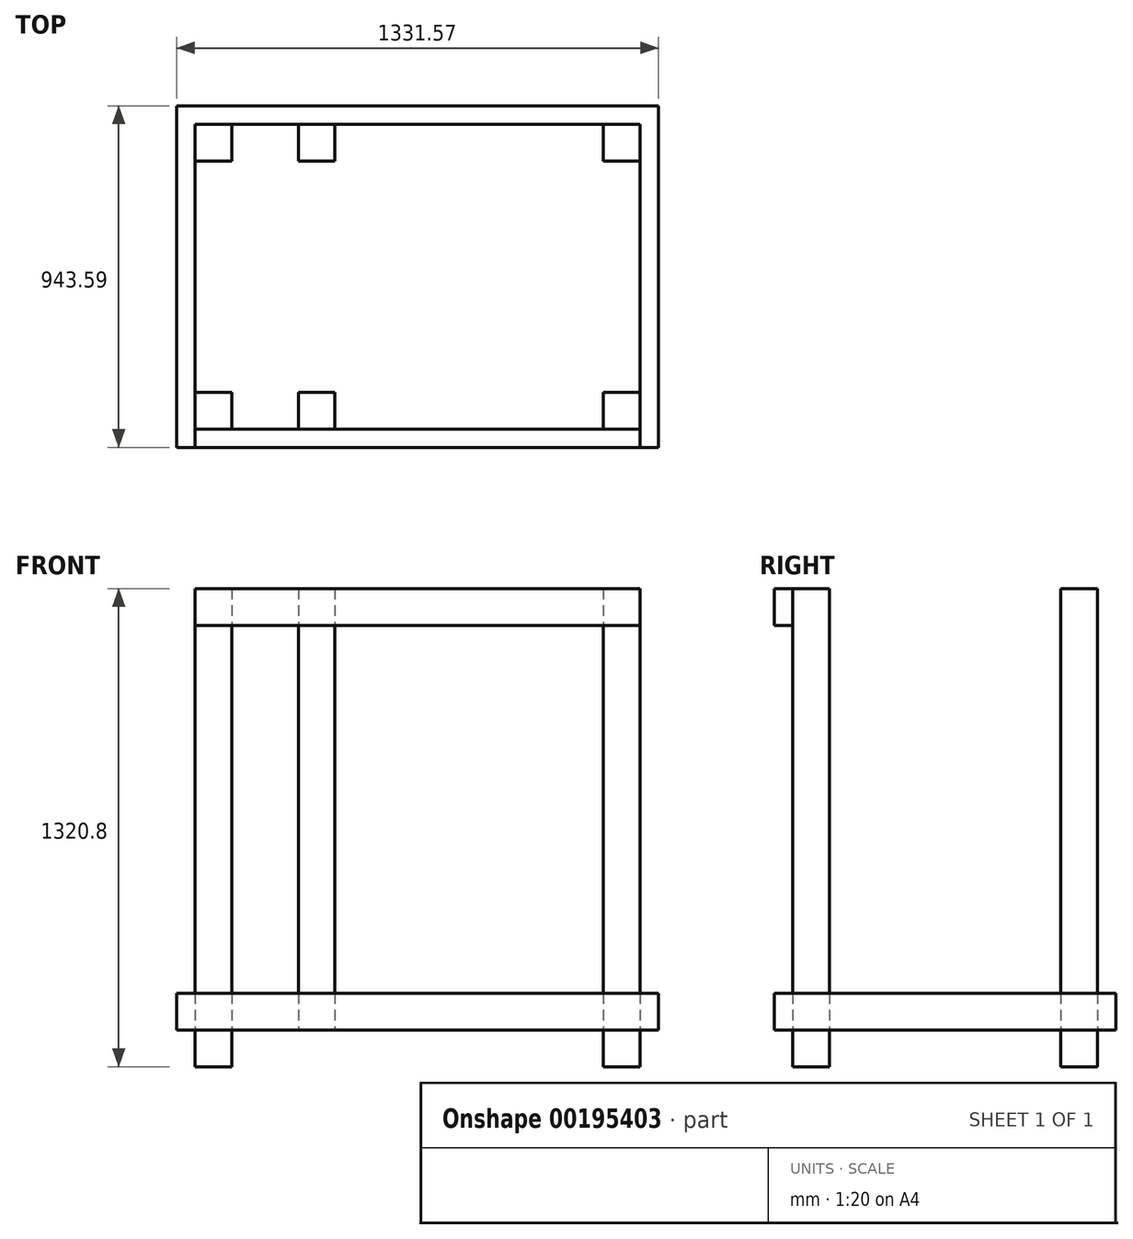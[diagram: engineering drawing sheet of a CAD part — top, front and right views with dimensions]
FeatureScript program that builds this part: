
annotation { "Feature Type Name" : "Feature", "Feature Type Description" : "" }
export const myFeature = defineFeature(function(context is Context, id is Id, definition is map)
    precondition{}
    {
        {
            var Q0;
            Q0=qCreatedBy(makeId("Top.planeOp"),FACE);
            var sketch = newSketch(context, id + "F0", { "sketchPlane" : qUnion([Q0])});
            skLineSegment(sketch, "E0.bottom", {"start": v(0, 0) * mm, "end": v(101.6, 0) * mm});
            skLineSegment(sketch, "E0.top", {"start": v(0, -101.6) * mm, "end": v(101.6, -101.6) * mm});
            skLineSegment(sketch, "E0.left", {"start": v(0, 0) * mm, "end": v(0, -101.6) * mm});
            skLineSegment(sketch, "E0.right", {"start": v(101.6, 0) * mm, "end": v(101.6, -101.6) * mm});
            skLineSegment(sketch, "E1.bottom", {"start": v(0, -740.39) * mm, "end": v(101.6, -740.39) * mm});
            skLineSegment(sketch, "E1.top", {"start": v(0, -841.99) * mm, "end": v(101.6, -841.99) * mm});
            skLineSegment(sketch, "E1.left", {"start": v(0, -740.39) * mm, "end": v(0, -841.99) * mm});
            skLineSegment(sketch, "E1.right", {"start": v(101.6, -740.39) * mm, "end": v(101.6, -841.99) * mm});
            skLineSegment(sketch, "E2.bottom", {"start": v(1128.37, -740.39) * mm, "end": v(1229.97, -740.39) * mm});
            skLineSegment(sketch, "E2.top", {"start": v(1128.37, -841.99) * mm, "end": v(1229.97, -841.99) * mm});
            skLineSegment(sketch, "E2.left", {"start": v(1128.37, -740.39) * mm, "end": v(1128.37, -841.99) * mm});
            skLineSegment(sketch, "E2.right", {"start": v(1229.97, -740.39) * mm, "end": v(1229.97, -841.99) * mm});
            skLineSegment(sketch, "E3.bottom", {"start": v(1128.37, -101.6) * mm, "end": v(1229.97, -101.6) * mm});
            skLineSegment(sketch, "E3.top", {"start": v(1128.37, 0) * mm, "end": v(1229.97, 0) * mm});
            skLineSegment(sketch, "E3.left", {"start": v(1128.37, -101.6) * mm, "end": v(1128.37, 0) * mm});
            skLineSegment(sketch, "E3.right", {"start": v(1229.97, -101.6) * mm, "end": v(1229.97, 0) * mm});
            skLineSegment(sketch, "E4.bottom", {"start": v(285.44, -740.39) * mm, "end": v(387.04, -740.39) * mm});
            skLineSegment(sketch, "E4.top", {"start": v(285.44, -841.99) * mm, "end": v(387.04, -841.99) * mm});
            skLineSegment(sketch, "E4.left", {"start": v(285.44, -740.39) * mm, "end": v(285.44, -841.99) * mm});
            skLineSegment(sketch, "E4.right", {"start": v(387.04, -740.39) * mm, "end": v(387.04, -841.99) * mm});
            skLineSegment(sketch, "E5.bottom", {"start": v(285.44, -101.6) * mm, "end": v(387.04, -101.6) * mm});
            skLineSegment(sketch, "E5.top", {"start": v(285.44, 0) * mm, "end": v(387.04, 0) * mm});
            skLineSegment(sketch, "E5.left", {"start": v(285.44, -101.6) * mm, "end": v(285.44, 0) * mm});
            skLineSegment(sketch, "E5.right", {"start": v(387.04, -101.6) * mm, "end": v(387.04, 0) * mm});
            skLineSegment(sketch, "E6.bottom", {"start": v(0, 0) * mm, "end": v(1229.97, 0) * mm});
            skLineSegment(sketch, "E6.top", {"start": v(0, 50.8) * mm, "end": v(1229.97, 50.8) * mm});
            skLineSegment(sketch, "E6.left", {"start": v(0, 0) * mm, "end": v(0, 50.8) * mm});
            skLineSegment(sketch, "E6.right", {"start": v(1229.97, 0) * mm, "end": v(1229.97, 50.8) * mm});
            skLineSegment(sketch, "E7.bottom", {"start": v(0, -841.99) * mm, "end": v(1229.97, -841.99) * mm});
            skLineSegment(sketch, "E7.top", {"start": v(0, -892.79) * mm, "end": v(1229.97, -892.79) * mm});
            skLineSegment(sketch, "E7.left", {"start": v(0, -841.99) * mm, "end": v(0, -892.79) * mm});
            skLineSegment(sketch, "E7.right", {"start": v(1229.97, -841.99) * mm, "end": v(1229.97, -892.79) * mm});
            skLineSegment(sketch, "E8.bottom", {"start": v(1229.97, 50.8) * mm, "end": v(1280.77, 50.8) * mm});
            skLineSegment(sketch, "E8.top", {"start": v(1229.97, -892.79) * mm, "end": v(1280.77, -892.79) * mm});
            skLineSegment(sketch, "E8.left", {"start": v(1229.97, 50.8) * mm, "end": v(1229.97, -892.79) * mm});
            skLineSegment(sketch, "E8.right", {"start": v(1280.77, 50.8) * mm, "end": v(1280.77, -892.79) * mm});
            skLineSegment(sketch, "E9.bottom", {"start": v(0, 50.8) * mm, "end": v(-50.8, 50.8) * mm});
            skLineSegment(sketch, "E9.top", {"start": v(0, -892.79) * mm, "end": v(-50.8, -892.79) * mm});
            skLineSegment(sketch, "E9.left", {"start": v(0, 50.8) * mm, "end": v(0, -892.79) * mm});
            skLineSegment(sketch, "E9.right", {"start": v(-50.8, 50.8) * mm, "end": v(-50.8, -892.79) * mm});
            skLineSegment(sketch, "E10.bottom", {"start": v(387.04, 0) * mm, "end": v(437.84, 0) * mm});
            skLineSegment(sketch, "E10.top", {"start": v(387.04, -841.99) * mm, "end": v(437.84, -841.99) * mm});
            skLineSegment(sketch, "E10.left", {"start": v(387.04, 0) * mm, "end": v(387.04, -841.99) * mm});
            skLineSegment(sketch, "E10.right", {"start": v(437.84, 0) * mm, "end": v(437.84, -841.99) * mm});
            skSolve(sketch);
        }
        {
            var Q0;
            {var subQ0=sQuery(id+"F0.wireOp",EDGE,"E1.bottom");Q0=makeQuery(id+"F0.imprint","IMPRINT",FACE,{"disambiguationData":[TD([[makeQuery(id+"F0.imprint","IMPRINT",EDGE,{"derivedFrom":subQ0}),-1.0]])]});}
            var Q1;
            {var subQ0=sQuery(id+"F0.wireOp",EDGE,"E0.top");Q1=makeQuery(id+"F0.imprint","IMPRINT",FACE,{"disambiguationData":[TD([[makeQuery(id+"F0.imprint","IMPRINT",EDGE,{"derivedFrom":subQ0}),1.0]])]});}
            var Q2;
            {var subQ0=sQuery(id+"F0.wireOp",EDGE,"E4.bottom");Q2=makeQuery(id+"F0.imprint","IMPRINT",FACE,{"disambiguationData":[TD([[makeQuery(id+"F0.imprint","IMPRINT",EDGE,{"derivedFrom":subQ0}),-1.0]])]});}
            var Q3;
            {var subQ0=sQuery(id+"F0.wireOp",EDGE,"E5.bottom");Q3=makeQuery(id+"F0.imprint","IMPRINT",FACE,{"disambiguationData":[TD([[makeQuery(id+"F0.imprint","IMPRINT",EDGE,{"derivedFrom":subQ0}),1.0]])]});}
            var Q4;
            {var subQ0=sQuery(id+"F0.wireOp",EDGE,"E3.bottom");Q4=makeQuery(id+"F0.imprint","IMPRINT",FACE,{"disambiguationData":[TD([[makeQuery(id+"F0.imprint","IMPRINT",EDGE,{"derivedFrom":subQ0}),1.0]])]});}
            var Q5;
            {var subQ0=sQuery(id+"F0.wireOp",EDGE,"E2.bottom");Q5=makeQuery(id+"F0.imprint","IMPRINT",FACE,{"disambiguationData":[TD([[makeQuery(id+"F0.imprint","IMPRINT",EDGE,{"derivedFrom":subQ0}),-1.0]])]});}
            extrude(context, id + "F1", {"entities" : qUnion([Q0, Q1, Q2, Q3, Q4, Q5]), "depth" : 1219.2 * mm});
        }
        {
            var Q0;
            {var subQ3=sQuery(id+"F0.wireOp",EDGE,"E9.bottom");Q0=makeQuery(id+"F0.imprint","IMPRINT",FACE,{"disambiguationData":[TD([[makeQuery(id+"F0.imprint","IMPRINT",EDGE,{"derivedFrom":subQ3}),1.0]])]});}
            var Q1;
            {var subQ9=sQuery(id+"F0.wireOp",EDGE,"E7.top");Q1=makeQuery(id+"F0.imprint","IMPRINT",FACE,{"disambiguationData":[TD([[makeQuery(id+"F0.imprint","IMPRINT",EDGE,{"derivedFrom":subQ9}),1.0]])]});}
            var Q2;
            {var subQ3=sQuery(id+"F0.wireOp",EDGE,"E8.bottom");Q2=makeQuery(id+"F0.imprint","IMPRINT",FACE,{"disambiguationData":[TD([[makeQuery(id+"F0.imprint","IMPRINT",EDGE,{"derivedFrom":subQ3}),-1.0]])]});}
            var Q3;
            {var subQ5=sQuery(id+"F0.wireOp",EDGE,"E6.top");Q3=makeQuery(id+"F0.imprint","IMPRINT",FACE,{"disambiguationData":[TD([[makeQuery(id+"F0.imprint","IMPRINT",EDGE,{"derivedFrom":subQ5}),-1.0]])]});}
            var Q4;
            {var subQ3=sQuery(id+"F0.wireOp",EDGE,"E10.bottom");Q4=makeQuery(id+"F0.imprint","IMPRINT",FACE,{"disambiguationData":[TD([[makeQuery(id+"F0.imprint","IMPRINT",EDGE,{"derivedFrom":subQ3}),-1.0]])]});}
            extrude(context, id + "F2", {"entities" : qUnion([Q0, Q1, Q2, Q3, Q4]), "depth" : 101.6 * mm});
        }
        {
            var Q0;
            {var subQ0=sQuery(id+"F0.wireOp",EDGE,"E1.bottom");Q0=makeQuery(id+"F0.imprint","IMPRINT",FACE,{"disambiguationData":[TD([[makeQuery(id+"F0.imprint","IMPRINT",EDGE,{"derivedFrom":subQ0}),-1.0]])]});}
            var Q1;
            {var subQ0=sQuery(id+"F0.wireOp",EDGE,"E0.top");Q1=makeQuery(id+"F0.imprint","IMPRINT",FACE,{"disambiguationData":[TD([[makeQuery(id+"F0.imprint","IMPRINT",EDGE,{"derivedFrom":subQ0}),1.0]])]});}
            var Q2;
            {var subQ0=sQuery(id+"F0.wireOp",EDGE,"E3.bottom");Q2=makeQuery(id+"F0.imprint","IMPRINT",FACE,{"disambiguationData":[TD([[makeQuery(id+"F0.imprint","IMPRINT",EDGE,{"derivedFrom":subQ0}),1.0]])]});}
            var Q3;
            {var subQ0=sQuery(id+"F0.wireOp",EDGE,"E2.bottom");Q3=makeQuery(id+"F0.imprint","IMPRINT",FACE,{"disambiguationData":[TD([[makeQuery(id+"F0.imprint","IMPRINT",EDGE,{"derivedFrom":subQ0}),-1.0]])]});}
            extrude(context, id + "F3", {"entities" : qUnion([Q0, Q1, Q2, Q3]), "oppositeDirection" : true, "depth" : 101.6 * mm});
        }
        {
            var Q0;
            Q0=makeQuery(id+"F1.opExtrude","CAP_FACE",FACE,{"disambiguationData":[OSD([sQuery(id+"F0.wireOp",EDGE,"E2.bottom"),sQuery(id+"F0.wireOp",EDGE,"E2.left"),sQuery(id+"F0.wireOp",EDGE,"E7.bottom"),sQuery(id+"F0.wireOp",EDGE,"E8.left")])],"isStart":false});
            var sketch = newSketch(context, id + "F4", { "sketchPlane" : qUnion([Q0])});
            skLineSegment(sketch, "E11.bottom", {"start": v(1229.97, -841.99) * mm, "end": v(0, -841.99) * mm});
            skLineSegment(sketch, "E11.top", {"start": v(1229.97, -892.79) * mm, "end": v(0, -892.79) * mm});
            skLineSegment(sketch, "E11.left", {"start": v(1229.97, -841.99) * mm, "end": v(1229.97, -892.79) * mm});
            skLineSegment(sketch, "E11.right", {"start": v(0, -841.99) * mm, "end": v(0, -892.79) * mm});
            skSolve(sketch);
        }
        {
            var Q0;
            Q0=makeQuery(id+"F4.imprint","IMPRINT",FACE,{"disambiguationData":[TD([[makeQuery(id+"F4.imprint","IMPRINT",EDGE,{"derivedFrom":sQuery(id+"F4.wireOp",EDGE,"E11.top")}),-1.0]])]});
            extrude(context, id + "F5", {"entities" : qUnion([Q0]), "oppositeDirection" : true, "depth" : 101.6 * mm});
        }
    });
